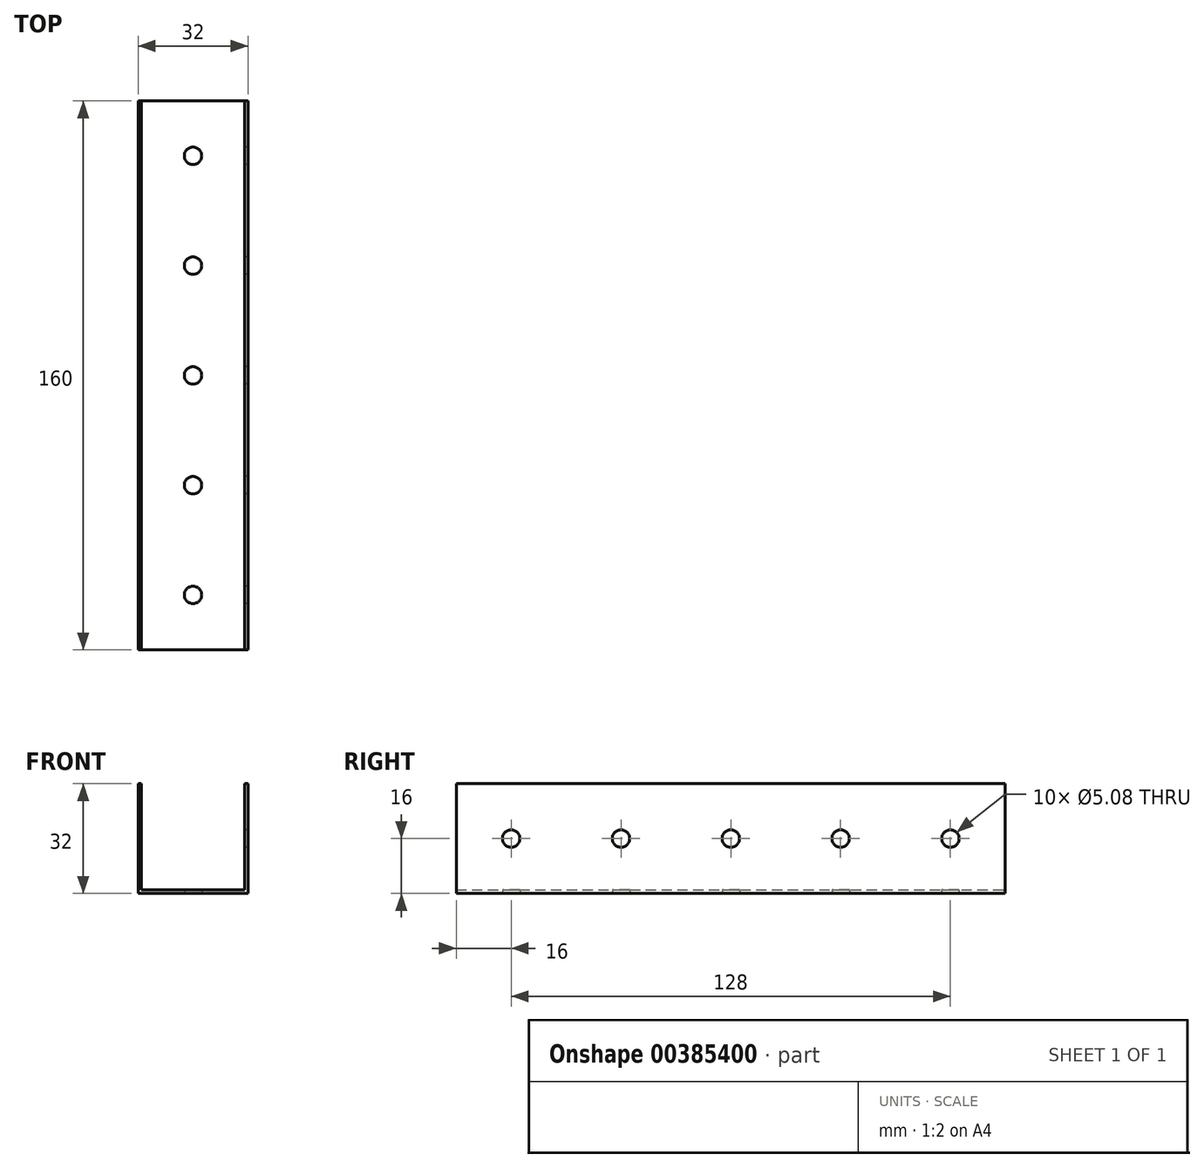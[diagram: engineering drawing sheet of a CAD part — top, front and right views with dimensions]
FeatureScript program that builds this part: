
annotation { "Feature Type Name" : "Feature", "Feature Type Description" : "" }
export const myFeature = defineFeature(function(context is Context, id is Id, definition is map)
    precondition{}
    {
        {
            var Q0;
            Q0=qCreatedBy(makeId("Front.planeOp"),FACE);
            var sketch = newSketch(context, id + "F0", { "sketchPlane" : qUnion([Q0])});
            skLineSegment(sketch, "E0", {"start": v(-16, 15.75) * mm, "end": v(-16, -16.25) * mm});
            skLineSegment(sketch, "E1", {"start": v(-16, -16.25) * mm, "end": v(16, -16.25) * mm});
            skLineSegment(sketch, "E2", {"start": v(16, -16.25) * mm, "end": v(16, 15.75) * mm});
            skLineSegment(sketch, "E3", {"start": v(16, 15.75) * mm, "end": v(15, 15.75) * mm});
            skLineSegment(sketch, "E4", {"start": v(15, 15.75) * mm, "end": v(15, -15.25) * mm});
            skLineSegment(sketch, "E5", {"start": v(15, -15.25) * mm, "end": v(-15, -15.25) * mm});
            skLineSegment(sketch, "E6", {"start": v(-15, -15.25) * mm, "end": v(-15, 15.75) * mm});
            skLineSegment(sketch, "E7", {"start": v(-15, 15.75) * mm, "end": v(-16, 15.75) * mm});
            skSolve(sketch);
        }
        {
            var Q0;
            Q0=qSketchRegion(id+"F0",true);
            extrude(context, id + "F1", {"entities" : qUnion([Q0]), "depth" : 160 * mm});
        }
        {
            var Q0;
            Q0=makeQuery(id+"F1.opExtrude","SWEPT_FACE",FACE,{"disambiguationData":[OSD([sQuery(id+"F0.wireOp",EDGE,"E0")])]});
            var sketch = newSketch(context, id + "F2", { "sketchPlane" : qUnion([Q0])});
            skPoint(sketch, "E8", {"position": v(32, 15.75) * mm});
            skPoint(sketch, "E9", {"position": v(64, 15.75) * mm});
            skPoint(sketch, "E10", {"position": v(96, 15.75) * mm});
            skLineSegment(sketch, "E11", {"start": v(32, 15.75) * mm, "end": v(0, 15.75) * mm});
            skPoint(sketch, "E12", {"position": v(128, 15.75) * mm});
            skPoint(sketch, "E13", {"position": v(32, -16.25) * mm});
            skPoint(sketch, "E14", {"position": v(64, -16.25) * mm});
            skPoint(sketch, "E15", {"position": v(96, -16.25) * mm});
            skPoint(sketch, "E16", {"position": v(128, -16.25) * mm});
            skPoint(sketch, "E17", {"position": v(16, -0.25) * mm});
            skPoint(sketch, "E18", {"position": v(48, -0.25) * mm});
            skPoint(sketch, "E19", {"position": v(80, -0.25) * mm});
            skPoint(sketch, "E20", {"position": v(112, -0.25) * mm});
            skPoint(sketch, "E21", {"position": v(144, -0.25) * mm});
            skCircle(sketch, "E22", {"center": v(16, -0.25) * mm, "radius": 2.54 * mm});
            skCircle(sketch, "E23", {"center": v(48, -0.25) * mm, "radius": 2.54 * mm});
            skCircle(sketch, "E24", {"center": v(80, -0.25) * mm, "radius": 2.54 * mm});
            skCircle(sketch, "E25", {"center": v(112, -0.25) * mm, "radius": 2.54 * mm});
            skCircle(sketch, "E26", {"center": v(144, -0.25) * mm, "radius": 2.54 * mm});
            skSolve(sketch);
        }
        {
            var Q0;
            Q0=qSketchRegion(id+"F2",true);
            extrude(context, id + "F3", {"entities" : qUnion([Q0]), "operationType" : NewBodyOperationType.REMOVE, "oppositeDirection" : true, "depth" : 50.8 * mm});
        }
        {
            var Q0;
            Q0=makeQuery(id+"F1.opExtrude","SWEPT_FACE",FACE,{"disambiguationData":[OSD([sQuery(id+"F0.wireOp",EDGE,"E1")])]});
            var sketch = newSketch(context, id + "F4", { "sketchPlane" : qUnion([Q0])});
            skPoint(sketch, "E27.0", {"position": v(-16, 128) * mm});
            skPoint(sketch, "E28.0", {"position": v(-16, 96) * mm});
            skPoint(sketch, "E29.0", {"position": v(-16, 64) * mm});
            skPoint(sketch, "E30.0", {"position": v(-16, 32) * mm});
            skPoint(sketch, "E31", {"position": v(16, 128) * mm});
            skPoint(sketch, "E32", {"position": v(16, 96) * mm});
            skPoint(sketch, "E33", {"position": v(16, 64) * mm});
            skPoint(sketch, "E34", {"position": v(16, 32) * mm});
            skPoint(sketch, "E35", {"position": v(0, 144) * mm});
            skPoint(sketch, "E36", {"position": v(0, 112) * mm});
            skPoint(sketch, "E37", {"position": v(0, 80) * mm});
            skPoint(sketch, "E38", {"position": v(0, 48) * mm});
            skPoint(sketch, "E39", {"position": v(0, 16) * mm});
            skCircle(sketch, "E40", {"center": v(0, 144) * mm, "radius": 2.54 * mm});
            skCircle(sketch, "E41", {"center": v(0, 112) * mm, "radius": 2.54 * mm});
            skCircle(sketch, "E42", {"center": v(0, 80) * mm, "radius": 2.54 * mm});
            skCircle(sketch, "E43", {"center": v(0, 48) * mm, "radius": 2.54 * mm});
            skCircle(sketch, "E44", {"center": v(0, 16) * mm, "radius": 2.54 * mm});
            skSolve(sketch);
        }
        {
            var Q0;
            Q0=qSketchRegion(id+"F4",true);
            extrude(context, id + "F5", {"entities" : qUnion([Q0]), "operationType" : NewBodyOperationType.REMOVE, "oppositeDirection" : true, "depth" : 25.4 * mm});
        }
    });
